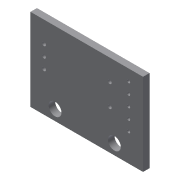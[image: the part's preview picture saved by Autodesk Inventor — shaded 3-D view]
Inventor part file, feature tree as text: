
AUTODESK INVENTOR PART (.ipt)
format: ipt  version: 2014 (Build 180170000, 170)  size: 117,248 bytes
history: native  units: in
note: dims shown in document units (in); Inventor stores cm internally (conversion verified against a paired STEP export)
features: reference x3, sketch x2, extrude x1, hole x1
ambient origin geometry x8: Origin, YZ Plane, XZ Plane, XY Plane, X Axis, Y Axis, Z Axis, Center Point
bodies: Solid1 (feature_tree)
feature tree (7):
  extrude  "Extrusion1"  Depth=0.761in
  hole  "Hole1"  [1 undecoded]
  sketch  "Sketch1"  dims[d0=1.04in d1=0.761in]
  sketch  "Sketch3"  dims[d2=0.1181in d3=0.1181in d4=0.227in d5=0.097in d6=0.548in d7=0.265in d8=0.095in d9=0.5in d10=0.208in d11=0.086in d12=0.05in d14=0.1in d15=0.1in d16=0.1in d18=0.0475in d19=0.1in d20=0.03in d21=0.03in d22=0.03in d23=0.03in d24=0.03in d25=0.035in d26=0.035in d27=0.035in d28=0.194in d29=0.1in d30=0.1in d31=0.125in d32=0.06in d33=0.0in d41=0.035in d42=0.75in d43=0.375in d44=0.25in d45=0.5635in d46=1.0in d47=0.8108in]
  reference  "Reference1"
  reference  "Reference2"
  reference  "Reference3"
note: 1 required parameter value undecoded (feature->parameter linkage not recoverable at this tier; creation-order binding heuristic only, values carry confidence <= 0.55)
